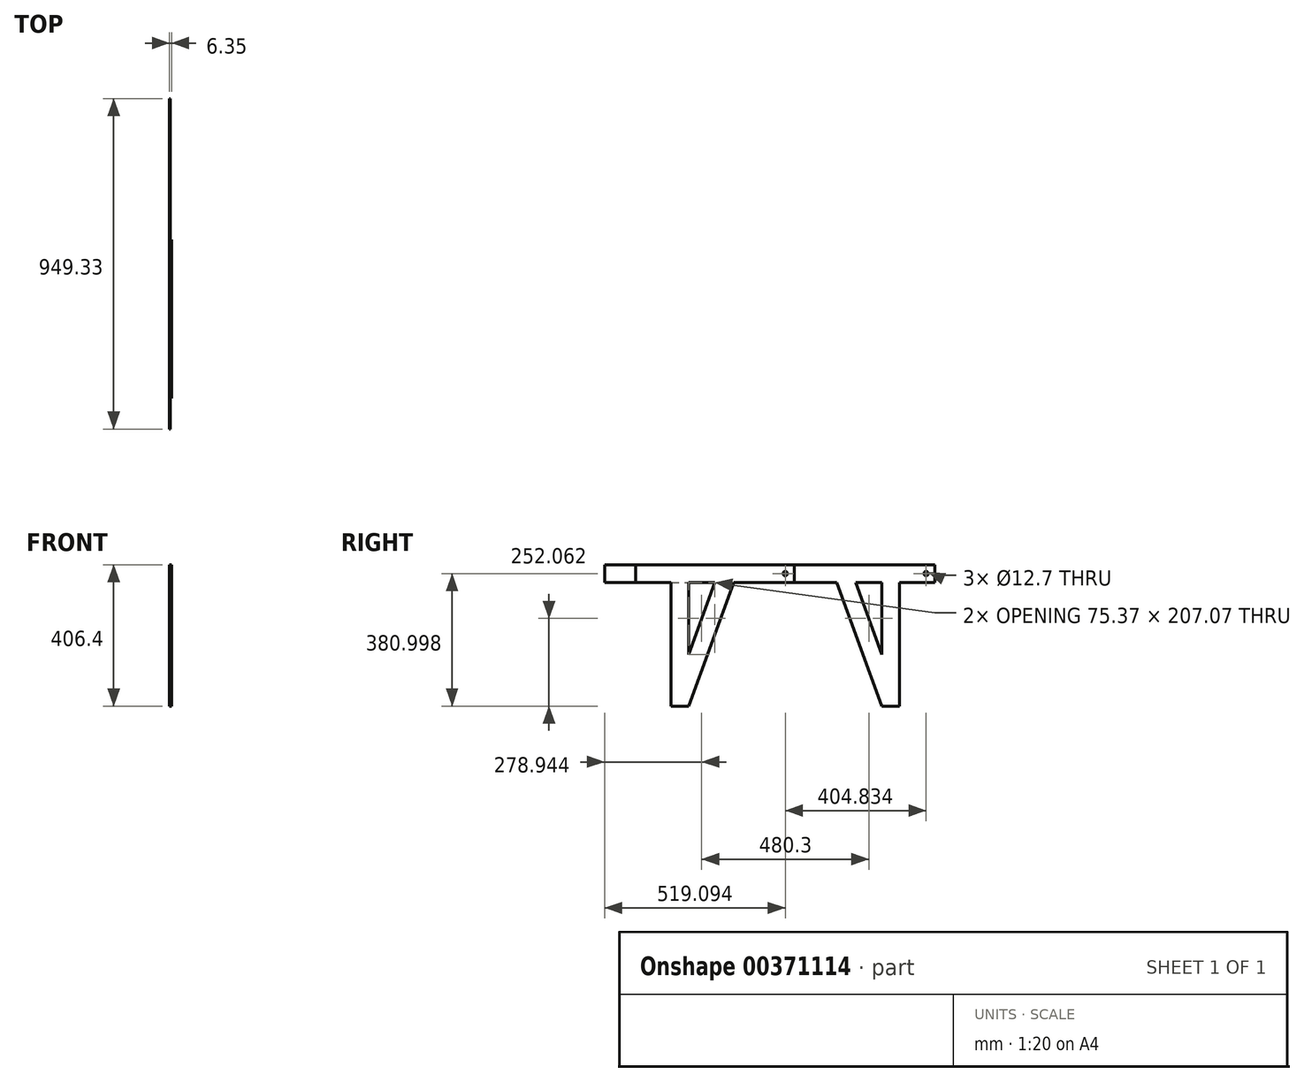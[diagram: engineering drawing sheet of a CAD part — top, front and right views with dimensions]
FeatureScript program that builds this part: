
annotation { "Feature Type Name" : "Feature", "Feature Type Description" : "" }
export const myFeature = defineFeature(function(context is Context, id is Id, definition is map)
    precondition{}
    {
        {
            var Q0;
            Q0=qCreatedBy(makeId("Right.planeOp"),FACE);
            var sketch = newSketch(context, id + "F0", { "sketchPlane" : qUnion([Q0])});
            skLineSegment(sketch, "E0.bottom", {"start": v(-588.96, 209.37) * mm, "end": v(360.37, 209.37) * mm});
            skLineSegment(sketch, "E0.top", {"start": v(-588.96, 158.57) * mm, "end": v(78.54, 158.57) * mm});
            skLineSegment(sketch, "E0.left", {"start": v(-588.96, 209.37) * mm, "end": v(-588.96, 158.57) * mm});
            skLineSegment(sketch, "E0.right", {"start": v(360.37, 209.37) * mm, "end": v(360.37, 158.57) * mm});
            skLineSegment(sketch, "E1.top", {"start": v(207.97, -197.03) * mm, "end": v(258.77, -197.03) * mm});
            skLineSegment(sketch, "E1.left", {"start": v(207.97, 158.57) * mm, "end": v(207.97, -48.5) * mm});
            skLineSegment(sketch, "E1.right", {"start": v(258.77, 158.57) * mm, "end": v(258.77, -197.03) * mm});
            skLineSegment(sketch, "E2.left", {"start": v(78.54, 158.57) * mm, "end": v(207.97, -197.03) * mm});
            skLineSegment(sketch, "E2.right", {"start": v(132.6, 158.57) * mm, "end": v(207.97, -48.5) * mm});
            skLineSegment(sketch, "E3.trimOffspring", {"start": v(132.6, 158.57) * mm, "end": v(207.97, 158.57) * mm});
            skLineSegment(sketch, "E4.trimOffspring", {"start": v(258.77, 158.57) * mm, "end": v(360.37, 158.57) * mm});
            skLineSegment(sketch, "E5", {"start": v(132.6, 158.57) * mm, "end": v(84.86, 141.2) * mm, "construction": true});
            skLineSegment(sketch, "E6", {"start": v(233.37, -197.03) * mm, "end": v(233.37, 183.97) * mm, "construction": true});
            skLineSegment(sketch, "E7", {"start": v(233.37, 183.97) * mm, "end": v(360.37, 183.97) * mm, "construction": true});
            skCircle(sketch, "E8", {"center": v(334.97, 183.97) * mm, "radius": 6.35 * mm});
            skSolve(sketch);
        }
        {
            var Q0;
            Q0 = qSketchRegion(id + "F0", true);
            extrude(context, id + "F1", {"entities" : qUnion([Q0]), "depth" : 3.17 * mm});
        }
        {
            var Q0;
            Q0=makeQuery(id+"F1.opExtrude","CAP_FACE",FACE,{"disambiguationData":[OSD([sQuery(id+"F0.wireOp",EDGE,"E0.bottom"),sQuery(id+"F0.wireOp",EDGE,"E0.top"),sQuery(id+"F0.wireOp",EDGE,"E0.left"),sQuery(id+"F0.wireOp",EDGE,"E0.right"),sQuery(id+"F0.wireOp",EDGE,"E1.top"),sQuery(id+"F0.wireOp",EDGE,"E1.left"),sQuery(id+"F0.wireOp",EDGE,"E1.right"),sQuery(id+"F0.wireOp",EDGE,"E2.left"),sQuery(id+"F0.wireOp",EDGE,"E2.right"),sQuery(id+"F0.wireOp",EDGE,"E3.trimOffspring"),sQuery(id+"F0.wireOp",EDGE,"238dff0e-271b-4be5-b624-802031fdb64e.trimOffspring"),sQuery(id+"F0.wireOp",EDGE,"E4.trimOffspring"),sQuery(id+"F0.wireOp",EDGE,"E8")])],"isStart":false});
            var sketch = newSketch(context, id + "F2", { "sketchPlane" : qUnion([Q0])});
            skLineSegment(sketch, "E9", {"start": v(-347.7, -197.03) * mm, "end": v(-398.5, -197.03) * mm});
            skLineSegment(sketch, "E10", {"start": v(-398.5, -197.03) * mm, "end": v(-398.5, 158.57) * mm});
            skLineSegment(sketch, "E11", {"start": v(-398.5, 158.57) * mm, "end": v(-500.1, 158.57) * mm});
            skLineSegment(sketch, "E12", {"start": v(-500.1, 158.57) * mm, "end": v(-500.1, 209.37) * mm});
            skLineSegment(sketch, "E13", {"start": v(-500.1, 209.37) * mm, "end": v(-44.47, 209.37) * mm});
            skLineSegment(sketch, "E14", {"start": v(-44.47, 209.37) * mm, "end": v(-44.47, 158.57) * mm});
            skLineSegment(sketch, "E15", {"start": v(-44.47, 158.57) * mm, "end": v(-218.27, 158.57) * mm});
            skLineSegment(sketch, "E16", {"start": v(-218.27, 158.57) * mm, "end": v(-347.7, -197.03) * mm});
            skLineSegment(sketch, "E17", {"start": v(-347.7, -48.5) * mm, "end": v(-272.33, 158.57) * mm});
            skLineSegment(sketch, "E18", {"start": v(-272.33, 158.57) * mm, "end": v(-347.7, 158.57) * mm});
            skLineSegment(sketch, "E19", {"start": v(-347.7, 158.57) * mm, "end": v(-347.7, -48.5) * mm});
            skLineSegment(sketch, "E20", {"start": v(-272.33, 158.57) * mm, "end": v(-224.6, 141.2) * mm, "construction": true});
            skCircle(sketch, "E21", {"center": v(-69.87, 183.97) * mm, "radius": 6.35 * mm});
            skLineSegment(sketch, "E22", {"start": v(-347.7, -197.03) * mm, "end": v(-69.87, -197.03) * mm, "construction": true});
            skLineSegment(sketch, "E23", {"start": v(-69.87, -197.03) * mm, "end": v(207.97, -197.03) * mm, "construction": true});
            skSolve(sketch);
        }
        {
            var Q0;
            Q0 = qSketchRegion(id + "F2", true);
            extrude(context, id + "F3", {"entities" : qUnion([Q0]), "depth" : 3.17 * mm});
        }
        {
            var Q0;
            Q0=makeQuery(id+"F1.opExtrude","CAP_FACE",FACE,{"disambiguationData":[OSD([sQuery(id+"F0.wireOp",EDGE,"E0.bottom"),sQuery(id+"F0.wireOp",EDGE,"E0.top"),sQuery(id+"F0.wireOp",EDGE,"E0.left"),sQuery(id+"F0.wireOp",EDGE,"E0.right"),sQuery(id+"F0.wireOp",EDGE,"E1.top"),sQuery(id+"F0.wireOp",EDGE,"E1.left"),sQuery(id+"F0.wireOp",EDGE,"E1.right"),sQuery(id+"F0.wireOp",EDGE,"E2.left"),sQuery(id+"F0.wireOp",EDGE,"E2.right"),sQuery(id+"F0.wireOp",EDGE,"E3.trimOffspring"),sQuery(id+"F0.wireOp",EDGE,"E4.trimOffspring"),sQuery(id+"F0.wireOp",EDGE,"E8")])],"isStart":false});
            var sketch = newSketch(context, id + "F4", { "sketchPlane" : qUnion([Q0])});
            skCircle(sketch, "E24.0", {"center": v(-69.87, 183.97) * mm, "radius": 6.35 * mm});
            skSolve(sketch);
        }
        {
            var Q0;
            Q0 = qSketchRegion(id + "F4", true);
            extrude(context, id + "F5", {"entities" : qUnion([Q0]), "operationType" : NewBodyOperationType.REMOVE, "oppositeDirection" : true, "depth" : 25.4 * mm});
        }
    });
